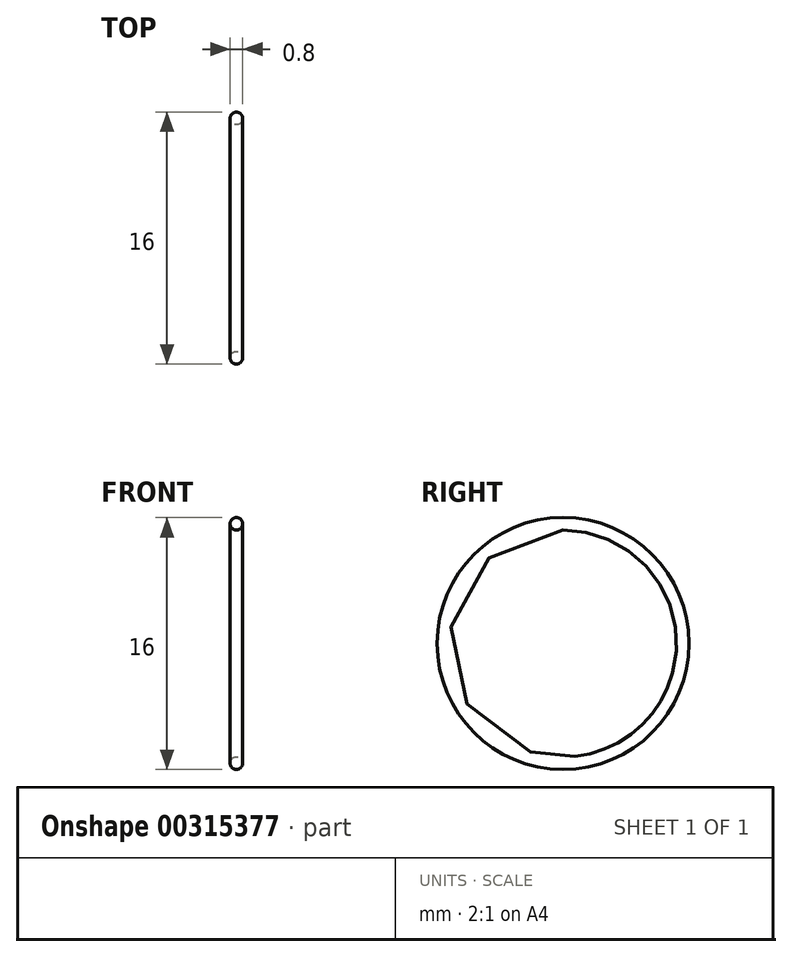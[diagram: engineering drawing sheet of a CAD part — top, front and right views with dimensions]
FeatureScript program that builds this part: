
annotation { "Feature Type Name" : "Feature", "Feature Type Description" : "" }
export const myFeature = defineFeature(function(context is Context, id is Id, definition is map)
    precondition{}
    {
        {
            var Q0;
            Q0=qCreatedBy(makeId("Front.planeOp"),FACE);
            var sketch = newSketch(context, id + "F0", { "sketchPlane" : qUnion([Q0])});
            skLineSegment(sketch, "E0", {"start": v(0, 0) * mm, "end": v(1.8, 0) * mm, "construction": true});
            skCircle(sketch, "E1", {"center": v(0, 7.6) * mm, "radius": 0.4 * mm});
            skSolve(sketch);
        }
        {
            var Q0;
            Q0 = qSketchRegion(id + "F0", true);
            var Q1;
            Q1=sQuery(id+"F0.wireOp",EDGE,"E0");
            revolve(context, id + "F1", {"entities" : qUnion([Q0]), "axis" : qUnion([Q1]), "revolveType" : RevolveType.FULL});
        }
    });
